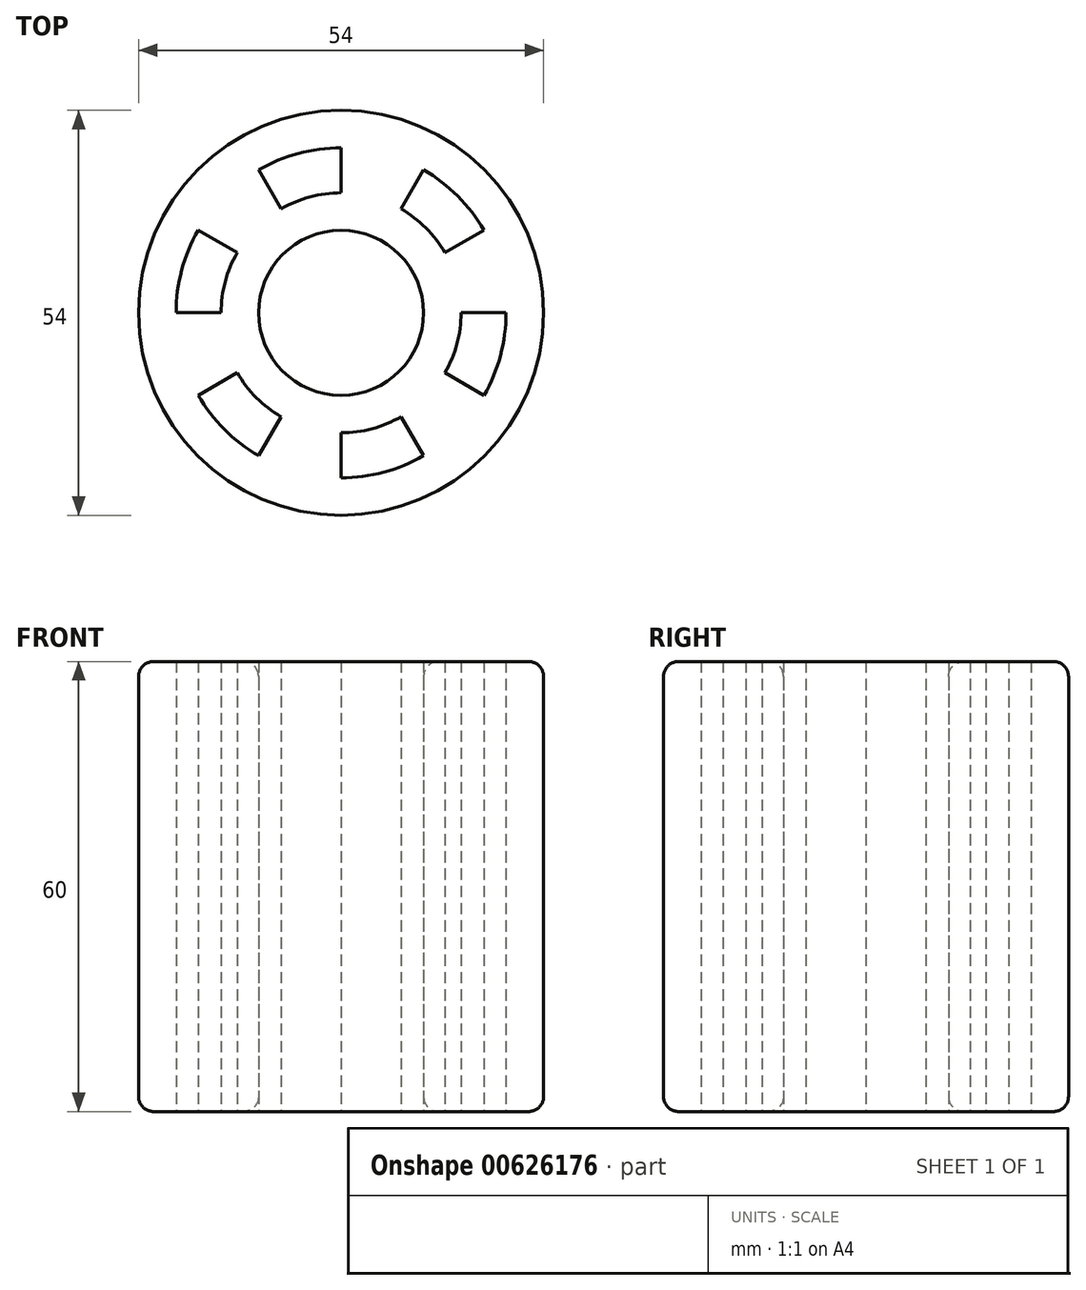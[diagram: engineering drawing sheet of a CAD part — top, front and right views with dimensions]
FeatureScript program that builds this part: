
annotation { "Feature Type Name" : "Feature", "Feature Type Description" : "" }
export const myFeature = defineFeature(function(context is Context, id is Id, definition is map)
    precondition{}
    {
        {
            var Q0;
            Q0=qCreatedBy(makeId("Top.planeOp"),FACE);
            var sketch = newSketch(context, id + "F0", { "sketchPlane" : qUnion([Q0])});
            skCircle(sketch, "E0", {"center": v(0, 0) * mm, "radius": 11 * mm});
            skCircle(sketch, "E1", {"center": v(0, 0) * mm, "radius": 27 * mm});
            skLineSegment(sketch, "E2", {"start": v(0, 0) * mm, "end": v(0, 11) * mm});
            skLineSegment(sketch, "E3.1.0", {"start": v(0, 0) * mm, "end": v(-5.5, 9.53) * mm});
            skLineSegment(sketch, "E3.2.0", {"start": v(0, 0) * mm, "end": v(-9.53, 5.5) * mm});
            skLineSegment(sketch, "E3.3.0", {"start": v(0, 0) * mm, "end": v(-11, 0) * mm});
            skLineSegment(sketch, "E3.4.0", {"start": v(0, 0) * mm, "end": v(-9.53, -5.5) * mm});
            skLineSegment(sketch, "E3.5.0", {"start": v(0, 0) * mm, "end": v(-5.5, -9.53) * mm});
            skLineSegment(sketch, "E3.6.0", {"start": v(0, 0) * mm, "end": v(0, -11) * mm});
            skLineSegment(sketch, "E3.7.0", {"start": v(0, 0) * mm, "end": v(5.5, -9.53) * mm});
            skLineSegment(sketch, "E3.8.0", {"start": v(0, 0) * mm, "end": v(9.53, -5.5) * mm});
            skLineSegment(sketch, "E3.9.0", {"start": v(0, 0) * mm, "end": v(11, 0) * mm});
            skLineSegment(sketch, "E3.10.0", {"start": v(0, 0) * mm, "end": v(9.53, 5.5) * mm});
            skLineSegment(sketch, "E3.11.0", {"start": v(0, 0) * mm, "end": v(5.5, 9.53) * mm});
            skArc(sketch, "E4.0", {"start": v(0, 16) * mm, "mid": v(-4.14, 15.45) * mm, "end": v(-8, 13.86) * mm});
            skArc(sketch, "E5.0", {"start": v(0, 22) * mm, "mid": v(-5.7, 21.25) * mm, "end": v(-11, 19.05) * mm});
            skPoint(sketch, "E6.orphan", {"position": v(13.5, 23.38) * mm});
            skPoint(sketch, "E7.orphan", {"position": v(0, 27) * mm});
            skArc(sketch, "E8.trimOffspring", {"start": v(13.86, 8) * mm, "mid": v(11.31, 11.31) * mm, "end": v(8, 13.86) * mm});
            skArc(sketch, "E9.trimOffspring", {"start": v(19.05, 11) * mm, "mid": v(15.56, 15.56) * mm, "end": v(11, 19.05) * mm});
            skArc(sketch, "E10.trimOffspring", {"start": v(13.86, -8) * mm, "mid": v(15.45, -4.14) * mm, "end": v(16, 0) * mm});
            skArc(sketch, "E11.trimOffspring", {"start": v(19.05, -11) * mm, "mid": v(21.25, -5.7) * mm, "end": v(22, 0) * mm});
            skArc(sketch, "E12.trimOffspring", {"start": v(0, -16) * mm, "mid": v(4.14, -15.45) * mm, "end": v(8, -13.86) * mm});
            skArc(sketch, "E13.trimOffspring", {"start": v(0, -22) * mm, "mid": v(5.7, -21.25) * mm, "end": v(11, -19.05) * mm});
            skArc(sketch, "E14.trimOffspring", {"start": v(-13.86, -8) * mm, "mid": v(-11.31, -11.31) * mm, "end": v(-8, -13.86) * mm});
            skArc(sketch, "E15.trimOffspring", {"start": v(-19.05, -11) * mm, "mid": v(-15.56, -15.56) * mm, "end": v(-11, -19.05) * mm});
            skArc(sketch, "E16.trimOffspring", {"start": v(-13.86, 8) * mm, "mid": v(-15.45, 4.14) * mm, "end": v(-16, 0) * mm});
            skArc(sketch, "E17.trimOffspring", {"start": v(-19.05, 11) * mm, "mid": v(-21.25, 5.7) * mm, "end": v(-22, 0) * mm});
            skLineSegment(sketch, "E18.trimOffspring", {"start": v(-13.86, 8) * mm, "end": v(-19.05, 11) * mm});
            skLineSegment(sketch, "E19.trimOffspring", {"start": v(-16, 0) * mm, "end": v(-22, 0) * mm});
            skLineSegment(sketch, "E20.trimOffspring", {"start": v(-13.86, -8) * mm, "end": v(-19.05, -11) * mm});
            skLineSegment(sketch, "E21.trimOffspring", {"start": v(-8, -13.86) * mm, "end": v(-11, -19.05) * mm});
            skLineSegment(sketch, "E22.trimOffspring", {"start": v(0, -16) * mm, "end": v(0, -22) * mm});
            skLineSegment(sketch, "E23.trimOffspring", {"start": v(8, -13.86) * mm, "end": v(11, -19.05) * mm});
            skLineSegment(sketch, "E24.trimOffspring", {"start": v(13.86, -8) * mm, "end": v(19.05, -11) * mm});
            skLineSegment(sketch, "E25.trimOffspring", {"start": v(16, 0) * mm, "end": v(27, 0) * mm});
            skPoint(sketch, "E26.orphan", {"position": v(-13.5, 23.38) * mm});
            skPoint(sketch, "E27.orphan", {"position": v(-23.38, 13.5) * mm});
            skPoint(sketch, "E28.orphan", {"position": v(-27, 0) * mm});
            skPoint(sketch, "E29.orphan", {"position": v(-23.38, -13.5) * mm});
            skPoint(sketch, "E30.orphan", {"position": v(-13.5, -23.38) * mm});
            skPoint(sketch, "E31.orphan", {"position": v(0, -27) * mm});
            skPoint(sketch, "E32.orphan", {"position": v(13.5, -23.38) * mm});
            skPoint(sketch, "E33.orphan", {"position": v(23.38, -13.5) * mm});
            skPoint(sketch, "E34.orphan", {"position": v(23.38, 13.5) * mm});
            skLineSegment(sketch, "E35.trimOffspring", {"start": v(-8, 13.86) * mm, "end": v(-11, 19.05) * mm});
            skLineSegment(sketch, "E36.trimOffspring", {"start": v(0, 16) * mm, "end": v(0, 22) * mm});
            skLineSegment(sketch, "E37.trimOffspring", {"start": v(8, 13.86) * mm, "end": v(11, 19.05) * mm});
            skLineSegment(sketch, "E38.trimOffspring", {"start": v(13.86, 8) * mm, "end": v(19.05, 11) * mm});
            skSolve(sketch);
        }
        {
            var Q0;
            Q0=makeQuery(id+"F0.imprint","IMPRINT",FACE,{"disambiguationData":[TD([[makeQuery(id+"F0.imprint","IMPRINT",EDGE,{"derivedFrom":sQuery(id+"F0.wireOp",EDGE,"E1")}),1.0]])]});
            extrude(context, id + "F1", {"entities" : qUnion([Q0]), "depth" : 60 * mm, "offsetDistance" : 25 * mm});
        }
        {
            var Q0;
            Q0=makeQuery(id+"F1.opExtrude","CAP_EDGE",EDGE,{"disambiguationData":[OSD([sQuery(id+"F0.wireOp",EDGE,"E1")])],"isStart":false});
            var Q1;
            Q1=makeQuery(id+"F1.opExtrude","CAP_EDGE",EDGE,{"disambiguationData":[OSD([sQuery(id+"F0.wireOp",EDGE,"E0")])],"isStart":false});
            var Q2;
            Q2=makeQuery(id+"F1.opExtrude","CAP_EDGE",EDGE,{"disambiguationData":[OSD([sQuery(id+"F0.wireOp",EDGE,"E1")])],"isStart":true});
            var Q3;
            Q3=makeQuery(id+"F1.opExtrude","CAP_EDGE",EDGE,{"disambiguationData":[OSD([sQuery(id+"F0.wireOp",EDGE,"E0")])],"isStart":true});
            fillet(context, id + "F2", {"entities" : qUnion([Q0, Q1, Q2, Q3]), "radius" : 2 * mm, "tangentPropagation" : true, "allowEdgeOverflow" : false});
        }
    });
